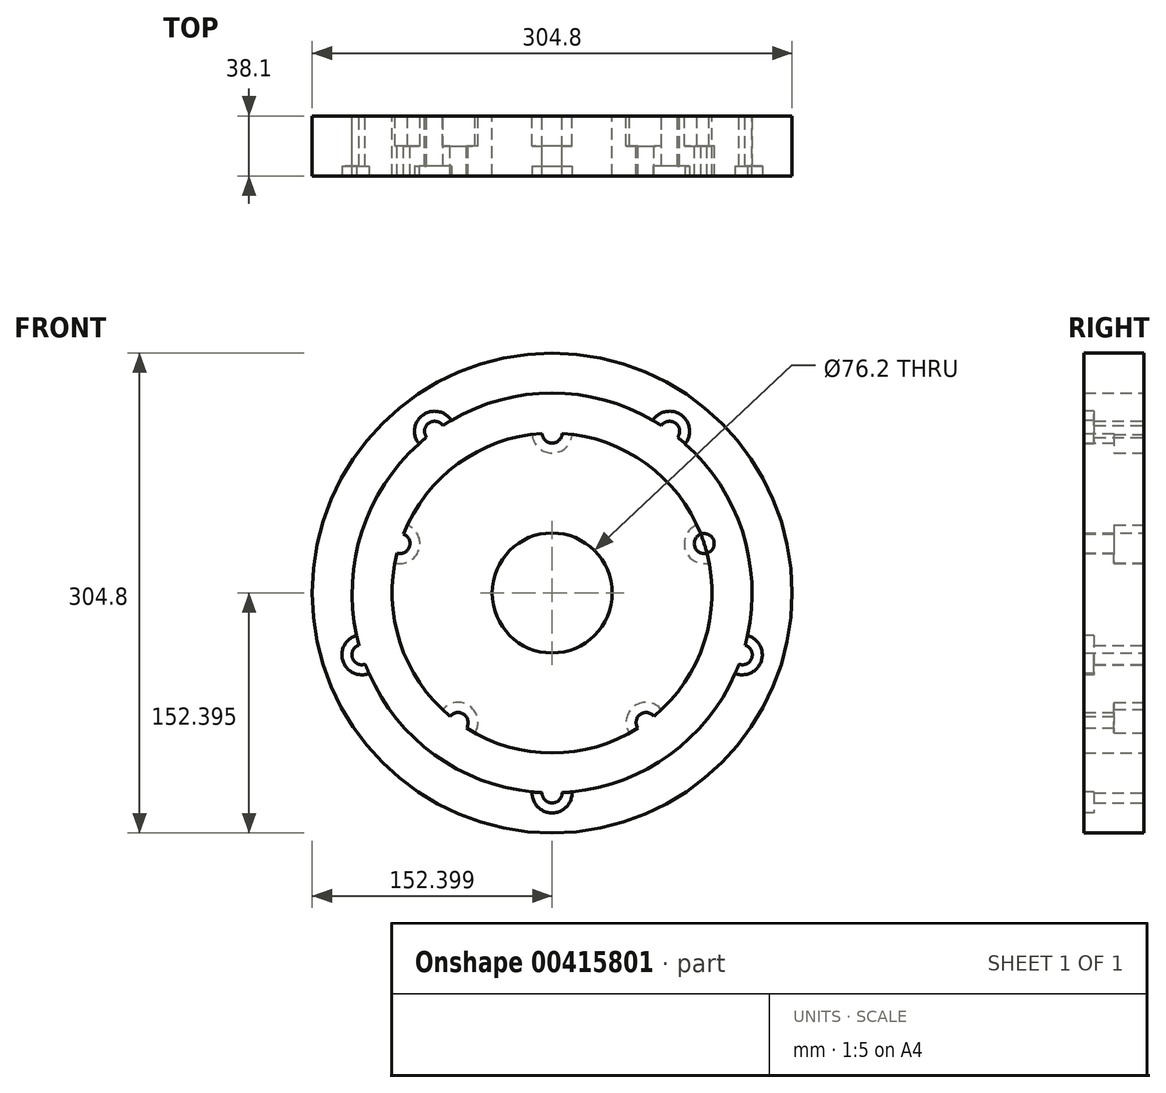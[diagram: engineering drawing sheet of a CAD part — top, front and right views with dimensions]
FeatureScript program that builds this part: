
annotation { "Feature Type Name" : "Feature", "Feature Type Description" : "" }
export const myFeature = defineFeature(function(context is Context, id is Id, definition is map)
    precondition{}
    {
        {
            var Q0;
            Q0=qCreatedBy(makeId("Front.planeOp"),FACE);
            var sketch = newSketch(context, id + "F0", { "sketchPlane" : qUnion([Q0])});
            skCircle(sketch, "E0", {"center": v(-14.28, 39.25) * mm, "radius": 152.4 * mm});
            skCircle(sketch, "E1", {"center": v(-14.28, 39.25) * mm, "radius": 38.1 * mm});
            skCircle(sketch, "E2", {"center": v(-14.28, 39.25) * mm, "radius": 101.6 * mm});
            skPoint(sketch, "E3", {"position": v(-14.28, 140.85) * mm});
            skPoint(sketch, "E4", {"position": v(-110.9, 70.64) * mm});
            skPoint(sketch, "E5", {"position": v(-74, -42.95) * mm});
            skPoint(sketch, "E6", {"position": v(45.44, -42.95) * mm});
            skPoint(sketch, "E7", {"position": v(82.35, 70.64) * mm});
            skCircle(sketch, "E8", {"center": v(-14.28, 39.25) * mm, "radius": 127 * mm});
            skPoint(sketch, "E9", {"position": v(-88.93, 142) * mm});
            skPoint(sketch, "E10", {"position": v(-135.06, 0) * mm});
            skPoint(sketch, "E11", {"position": v(-14.28, -87.75) * mm});
            skPoint(sketch, "E12", {"position": v(106.5, 0) * mm});
            skPoint(sketch, "E13", {"position": v(60.37, 142) * mm});
            skCircle(sketch, "E14", {"center": v(-14.28, 140.85) * mm, "radius": 6.35 * mm});
            skCircle(sketch, "E15", {"center": v(60.37, 142) * mm, "radius": 6.35 * mm});
            skCircle(sketch, "E16", {"center": v(82.35, 70.64) * mm, "radius": 6.35 * mm});
            skCircle(sketch, "E17", {"center": v(106.5, 0) * mm, "radius": 6.35 * mm});
            skCircle(sketch, "E18", {"center": v(45.44, -42.95) * mm, "radius": 6.35 * mm});
            skCircle(sketch, "E19", {"center": v(-14.28, -87.75) * mm, "radius": 6.35 * mm});
            skCircle(sketch, "E20", {"center": v(-74, -42.95) * mm, "radius": 6.35 * mm});
            skCircle(sketch, "E21", {"center": v(-135.06, 0) * mm, "radius": 6.35 * mm});
            skCircle(sketch, "E22", {"center": v(-110.9, 70.64) * mm, "radius": 6.35 * mm});
            skCircle(sketch, "E23", {"center": v(-88.93, 142) * mm, "radius": 6.35 * mm});
            skSolve(sketch);
        }
        {
            var Q0;
            Q0=qSketchRegion(id+"F0",true);
            var Q1;
            {var subQ8=sQuery(id+"F0.wireOp",EDGE,"E16");var subQ9=sQuery(id+"F0.wireOp",EDGE,"E2");var subQ10=makeQuery(id+"F0.imprint","INTERSECT",VERTEX,{"disambiguationData":[OD(0.0)],"derivedFrom":[subQ9,subQ8]});Q1=makeQuery(id+"F0.imprint","IMPRINT",FACE,{"disambiguationData":[TD([[makeQuery(id+"F0.imprint","IMPRINT",EDGE,{"disambiguationData":[TD([[subQ10,-1.0]])],"derivedFrom":subQ9}),-1.0]])]});}
            var Q2;
            Q2=makeQuery(id+"F0.imprint","IMPRINT",FACE,{"disambiguationData":[TD([[makeQuery(id+"F0.imprint","IMPRINT",EDGE,{"derivedFrom":sQuery(id+"F0.wireOp",EDGE,"E1")}),-1.0]])]});
            extrude(context, id + "F1", {"entities" : qUnion([Q0, Q1, Q2]), "depth" : 38.1 * mm});
        }
        {
            var Q0;
            Q0=makeQuery(id+"F1.opExtrude","CAP_FACE",FACE,{"disambiguationData":[OSD([sQuery(id+"F0.wireOp",EDGE,"E0"),sQuery(id+"F0.wireOp",EDGE,"E1"),sQuery(id+"F0.wireOp",EDGE,"E14"),sQuery(id+"F0.wireOp",EDGE,"E15"),sQuery(id+"F0.wireOp",EDGE,"E16"),sQuery(id+"F0.wireOp",EDGE,"E17"),sQuery(id+"F0.wireOp",EDGE,"E18"),sQuery(id+"F0.wireOp",EDGE,"E19"),sQuery(id+"F0.wireOp",EDGE,"E20"),sQuery(id+"F0.wireOp",EDGE,"E21"),sQuery(id+"F0.wireOp",EDGE,"E22"),sQuery(id+"F0.wireOp",EDGE,"E23")])],"isStart":true});
            var sketch = newSketch(context, id + "F2", { "sketchPlane" : qUnion([Q0])});
            skCircle(sketch, "E24", {"center": v(14.28, 140.85) * mm, "radius": 12.7 * mm});
            skCircle(sketch, "E25", {"center": v(-82.35, 70.64) * mm, "radius": 12.7 * mm});
            skCircle(sketch, "E26", {"center": v(-45.44, -42.95) * mm, "radius": 12.7 * mm});
            skCircle(sketch, "E27", {"center": v(74, -42.95) * mm, "radius": 12.7 * mm});
            skCircle(sketch, "E28", {"center": v(110.9, 70.64) * mm, "radius": 12.7 * mm});
            skSolve(sketch);
        }
        {
            var Q0;
            Q0=qSketchRegion(id+"F2",true);
            extrude(context, id + "F3", {"entities" : qUnion([Q0]), "operationType" : NewBodyOperationType.REMOVE, "oppositeDirection" : true, "depth" : 19.05 * mm});
        }
        {
            var Q0;
            Q0=makeQuery(id+"F1.opExtrude","CAP_FACE",FACE,{"disambiguationData":[OSD([sQuery(id+"F0.wireOp",EDGE,"E0"),sQuery(id+"F0.wireOp",EDGE,"E1"),sQuery(id+"F0.wireOp",EDGE,"E14"),sQuery(id+"F0.wireOp",EDGE,"E15"),sQuery(id+"F0.wireOp",EDGE,"E16"),sQuery(id+"F0.wireOp",EDGE,"E17"),sQuery(id+"F0.wireOp",EDGE,"E18"),sQuery(id+"F0.wireOp",EDGE,"E19"),sQuery(id+"F0.wireOp",EDGE,"E20"),sQuery(id+"F0.wireOp",EDGE,"E21"),sQuery(id+"F0.wireOp",EDGE,"E22"),sQuery(id+"F0.wireOp",EDGE,"E23")])],"isStart":false});
            var sketch = newSketch(context, id + "F4", { "sketchPlane" : qUnion([Q0])});
            skCircle(sketch, "E29", {"center": v(-88.93, 142) * mm, "radius": 12.7 * mm});
            skCircle(sketch, "E30", {"center": v(-135.06, 0) * mm, "radius": 12.7 * mm});
            skCircle(sketch, "E31", {"center": v(-14.28, -87.75) * mm, "radius": 12.7 * mm});
            skCircle(sketch, "E32", {"center": v(106.5, 0) * mm, "radius": 12.7 * mm});
            skCircle(sketch, "E33", {"center": v(60.37, 142) * mm, "radius": 12.7 * mm});
            skSolve(sketch);
        }
        {
            var Q0;
            Q0=qSketchRegion(id+"F4",true);
            extrude(context, id + "F5", {"entities" : qUnion([Q0]), "operationType" : NewBodyOperationType.REMOVE, "oppositeDirection" : true, "depth" : 6.35 * mm});
        }
    });
